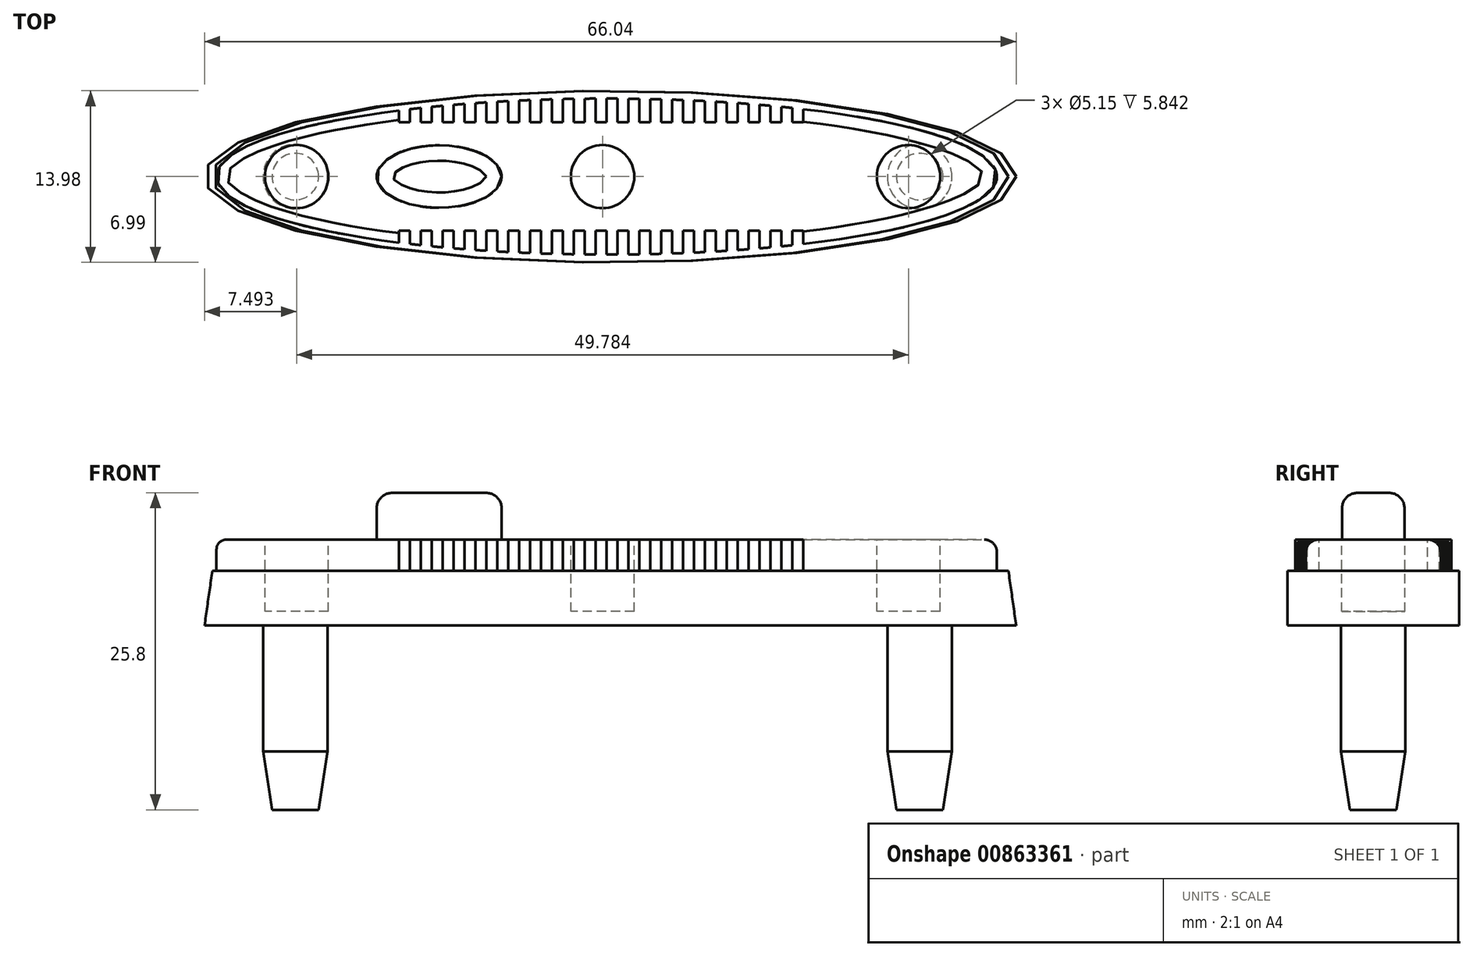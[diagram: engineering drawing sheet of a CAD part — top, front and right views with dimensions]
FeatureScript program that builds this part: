
annotation { "Feature Type Name" : "Feature", "Feature Type Description" : "" }
export const myFeature = defineFeature(function(context is Context, id is Id, definition is map)
    precondition{}
    {
        {
            var Q0;
            Q0=qCreatedBy(makeId("Top.planeOp"),FACE);
            var sketch = newSketch(context, id + "F0", { "sketchPlane" : qUnion([Q0])});
            skEllipse(sketch, "E0", {"center": v(0, 0) * mm, "majorRadius": 33.02 * mm, "minorRadius": 6.99 * mm, "majorAxis": v(1, 0)});
            skSolve(sketch);
        }
        {
            var Q0;
            Q0=qCreatedBy(makeId("Top.planeOp"),FACE);
            cPlane(context, id + "F1", {"entities" : qUnion([Q0]), "cplaneType" : CPlaneType.OFFSET, "offset" : 4.44 * mm, "width" : 152.4 * mm, "height" : 152.4 * mm});
        }
        {
            var Q0;
            Q0=qCreatedBy(id+"F1.planeOp",FACE);
            var sketch = newSketch(context, id + "F2", { "sketchPlane" : qUnion([Q0])});
            skEllipse(sketch, "E1", {"center": v(0, 0) * mm, "majorRadius": 32.39 * mm, "minorRadius": 6.99 * mm, "majorAxis": v(1, 0)});
            skSolve(sketch);
        }
        {
            var Q0;
            Q0=makeQuery(id+"F0.imprint","IMPRINT",FACE,{"disambiguationData":[TD([[makeQuery(id+"F0.imprint","IMPRINT",EDGE,{"derivedFrom":sQuery(id+"F0.wireOp",EDGE,"E0")}),1.0]])]});
            var Q1;
            Q1=makeQuery(id+"F2.imprint","IMPRINT",FACE,{"disambiguationData":[TD([[makeQuery(id+"F2.imprint","IMPRINT",EDGE,{"derivedFrom":sQuery(id+"F2.wireOp",EDGE,"E1")}),1.0]])]});
            loft(context, id + "F3", {"sheetProfilesArray" : [{ "sheetProfileEntities" : qUnion([Q0]) }, { "sheetProfileEntities" : qUnion([Q1]) }]});
        }
        {
            var Q0;
            Q0=makeQuery(id+"F3.opLoft","CAP_FACE",FACE,{"disambiguationData":[OSD([makeQuery(id+"F2.imprint","IMPRINT",FACE,{"disambiguationData":[TD([[makeQuery(id+"F2.imprint","IMPRINT",EDGE,{"derivedFrom":sQuery(id+"F2.wireOp",EDGE,"E1")}),1.0]])]})])],"isStart":true});
            var sketch = newSketch(context, id + "F4", { "sketchPlane" : qUnion([Q0])});
            skEllipse(sketch, "E2", {"center": v(-0.3, 0) * mm, "majorRadius": 31.75 * mm, "minorRadius": 6.35 * mm, "majorAxis": v(-1, 0)});
            skSolve(sketch);
        }
        {
            var Q0;
            Q0=makeQuery(id+"F4.imprint","IMPRINT",FACE,{"disambiguationData":[TD([[makeQuery(id+"F4.imprint","IMPRINT",EDGE,{"derivedFrom":sQuery(id+"F4.wireOp",EDGE,"E2")}),1.0]])]});
            extrude(context, id + "F5", {"entities" : qUnion([Q0]), "operationType" : NewBodyOperationType.ADD, "depth" : 2.54 * mm, "offsetDistance" : 25.4 * mm});
        }
        {
            var Q0;
            Q0=makeQuery(id+"F5.opExtrude","CAP_FACE",FACE,{"disambiguationData":[OSD([sQuery(id+"F4.wireOp",EDGE,"E2")])],"isStart":false});
            var sketch = newSketch(context, id + "F6", { "sketchPlane" : qUnion([Q0])});
            skPoint(sketch, "E3.oppositeSnap0", {"position": v(-0.3, 6.35) * mm});
            skLineSegment(sketch, "E3.bottom", {"start": v(-1.2, 4.4) * mm, "end": v(-0.3, 4.4) * mm});
            skLineSegment(sketch, "E3.top", {"start": v(-1.2, 7.13) * mm, "end": v(-0.3, 7.13) * mm});
            skLineSegment(sketch, "E3.left", {"start": v(-1.2, 4.4) * mm, "end": v(-1.2, 7.13) * mm});
            skLineSegment(sketch, "E3.right", {"start": v(-0.3, 4.4) * mm, "end": v(-0.3, 7.13) * mm});
            skPoint(sketch, "E4.1.0.0", {"position": v(1.48, 6.35) * mm});
            skLineSegment(sketch, "E4.1.0.1", {"start": v(1.48, 4.4) * mm, "end": v(1.48, 7.13) * mm});
            skLineSegment(sketch, "E4.1.0.2", {"start": v(0.57, 4.4) * mm, "end": v(1.48, 4.4) * mm});
            skLineSegment(sketch, "E4.1.0.3", {"start": v(0.57, 4.4) * mm, "end": v(0.57, 7.13) * mm});
            skLineSegment(sketch, "E4.1.0.4", {"start": v(0.57, 7.13) * mm, "end": v(1.48, 7.13) * mm});
            skPoint(sketch, "E4.2.0.0", {"position": v(3.26, 6.35) * mm});
            skLineSegment(sketch, "E4.2.0.1", {"start": v(3.26, 4.4) * mm, "end": v(3.26, 7.13) * mm});
            skLineSegment(sketch, "E4.2.0.2", {"start": v(2.35, 4.4) * mm, "end": v(3.26, 4.4) * mm});
            skLineSegment(sketch, "E4.2.0.3", {"start": v(2.35, 4.4) * mm, "end": v(2.35, 7.13) * mm});
            skLineSegment(sketch, "E4.2.0.4", {"start": v(2.35, 7.13) * mm, "end": v(3.26, 7.13) * mm});
            skPoint(sketch, "E4.3.0.0", {"position": v(5.04, 6.35) * mm});
            skLineSegment(sketch, "E4.3.0.1", {"start": v(5.04, 4.4) * mm, "end": v(5.04, 7.13) * mm});
            skLineSegment(sketch, "E4.3.0.2", {"start": v(4.13, 4.4) * mm, "end": v(5.04, 4.4) * mm});
            skLineSegment(sketch, "E4.3.0.3", {"start": v(4.13, 4.4) * mm, "end": v(4.13, 7.13) * mm});
            skLineSegment(sketch, "E4.3.0.4", {"start": v(4.13, 7.13) * mm, "end": v(5.04, 7.13) * mm});
            skPoint(sketch, "E4.4.0.0", {"position": v(6.81, 6.35) * mm});
            skLineSegment(sketch, "E4.4.0.1", {"start": v(6.81, 4.4) * mm, "end": v(6.81, 7.13) * mm});
            skLineSegment(sketch, "E4.4.0.2", {"start": v(5.9, 4.4) * mm, "end": v(6.81, 4.4) * mm});
            skLineSegment(sketch, "E4.4.0.3", {"start": v(5.9, 4.4) * mm, "end": v(5.9, 7.13) * mm});
            skLineSegment(sketch, "E4.4.0.4", {"start": v(5.9, 7.13) * mm, "end": v(6.81, 7.13) * mm});
            skPoint(sketch, "E4.5.0.0", {"position": v(8.6, 6.35) * mm});
            skLineSegment(sketch, "E4.5.0.1", {"start": v(8.6, 4.4) * mm, "end": v(8.6, 7.13) * mm});
            skLineSegment(sketch, "E4.5.0.2", {"start": v(7.68, 4.4) * mm, "end": v(8.6, 4.4) * mm});
            skLineSegment(sketch, "E4.5.0.3", {"start": v(7.68, 4.4) * mm, "end": v(7.68, 7.13) * mm});
            skLineSegment(sketch, "E4.5.0.4", {"start": v(7.68, 7.13) * mm, "end": v(8.6, 7.13) * mm});
            skPoint(sketch, "E4.6.0.0", {"position": v(10.37, 6.35) * mm});
            skLineSegment(sketch, "E4.6.0.1", {"start": v(10.37, 4.4) * mm, "end": v(10.37, 7.13) * mm});
            skLineSegment(sketch, "E4.6.0.2", {"start": v(9.46, 4.4) * mm, "end": v(10.37, 4.4) * mm});
            skLineSegment(sketch, "E4.6.0.3", {"start": v(9.46, 4.4) * mm, "end": v(9.46, 7.13) * mm});
            skLineSegment(sketch, "E4.6.0.4", {"start": v(9.46, 7.13) * mm, "end": v(10.37, 7.13) * mm});
            skPoint(sketch, "E4.7.0.0", {"position": v(12.15, 6.35) * mm});
            skLineSegment(sketch, "E4.7.0.1", {"start": v(12.15, 4.4) * mm, "end": v(12.15, 7.13) * mm});
            skLineSegment(sketch, "E4.7.0.2", {"start": v(11.24, 4.4) * mm, "end": v(12.15, 4.4) * mm});
            skLineSegment(sketch, "E4.7.0.3", {"start": v(11.24, 4.4) * mm, "end": v(11.24, 7.13) * mm});
            skLineSegment(sketch, "E4.7.0.4", {"start": v(11.24, 7.13) * mm, "end": v(12.15, 7.13) * mm});
            skPoint(sketch, "E4.8.0.0", {"position": v(13.93, 6.35) * mm});
            skLineSegment(sketch, "E4.8.0.1", {"start": v(13.93, 4.4) * mm, "end": v(13.93, 7.13) * mm});
            skLineSegment(sketch, "E4.8.0.2", {"start": v(13.02, 4.4) * mm, "end": v(13.93, 4.4) * mm});
            skLineSegment(sketch, "E4.8.0.3", {"start": v(13.02, 4.4) * mm, "end": v(13.02, 7.13) * mm});
            skLineSegment(sketch, "E4.8.0.4", {"start": v(13.02, 7.13) * mm, "end": v(13.93, 7.13) * mm});
            skPoint(sketch, "E4.9.0.0", {"position": v(15.7, 6.35) * mm});
            skLineSegment(sketch, "E4.9.0.1", {"start": v(15.7, 4.4) * mm, "end": v(15.7, 7.13) * mm});
            skLineSegment(sketch, "E4.9.0.2", {"start": v(14.8, 4.4) * mm, "end": v(15.7, 4.4) * mm});
            skLineSegment(sketch, "E4.9.0.3", {"start": v(14.8, 4.4) * mm, "end": v(14.8, 7.13) * mm});
            skLineSegment(sketch, "E4.9.0.4", {"start": v(14.8, 7.13) * mm, "end": v(15.7, 7.13) * mm});
            skLineSegment(sketch, "E4.direction1", {"start": v(-1.2, 4.4) * mm, "end": v(0.57, 4.4) * mm, "construction": true});
            skLineSegment(sketch, "E5", {"start": v(0, 0) * mm, "end": v(3.55, 0) * mm, "construction": true});
            skLineSegment(sketch, "E6", {"start": v(-0.75, 7.13) * mm, "end": v(-0.75, 4.39) * mm, "construction": true});
            skLineSegment(sketch, "E7.MirrorCS", {"start": v(-0.3, 7.13) * mm, "end": v(-1.2, 7.13) * mm});
            skLineSegment(sketch, "E8.MirrorCS", {"start": v(-5.63, 4.4) * mm, "end": v(-6.54, 4.4) * mm});
            skLineSegment(sketch, "E9.MirrorCS", {"start": v(-14.52, 4.4) * mm, "end": v(-15.43, 4.4) * mm});
            skLineSegment(sketch, "E10.MirrorCS", {"start": v(-16.3, 7.13) * mm, "end": v(-17.21, 7.13) * mm});
            skLineSegment(sketch, "E11.MirrorCS", {"start": v(-3.85, 7.13) * mm, "end": v(-4.76, 7.13) * mm});
            skLineSegment(sketch, "E12.MirrorCS", {"start": v(-9.19, 7.13) * mm, "end": v(-10.1, 7.13) * mm});
            skLineSegment(sketch, "E13.MirrorCS", {"start": v(-2.08, 7.13) * mm, "end": v(-2.99, 7.13) * mm});
            skLineSegment(sketch, "E14.MirrorCS", {"start": v(-16.3, 4.4) * mm, "end": v(-17.21, 4.4) * mm});
            skLineSegment(sketch, "E15.MirrorCS", {"start": v(-12.74, 4.4) * mm, "end": v(-13.65, 4.4) * mm});
            skLineSegment(sketch, "E16.MirrorCS", {"start": v(-14.52, 7.13) * mm, "end": v(-15.43, 7.13) * mm});
            skLineSegment(sketch, "E17.MirrorCS", {"start": v(-9.19, 4.4) * mm, "end": v(-10.1, 4.4) * mm});
            skLineSegment(sketch, "E18.MirrorCS", {"start": v(-12.74, 7.13) * mm, "end": v(-13.65, 7.13) * mm});
            skLineSegment(sketch, "E19.MirrorCS", {"start": v(-10.97, 4.4) * mm, "end": v(-11.88, 4.4) * mm});
            skLineSegment(sketch, "E20.MirrorCS", {"start": v(-3.85, 4.4) * mm, "end": v(-4.76, 4.4) * mm});
            skLineSegment(sketch, "E21.MirrorCS", {"start": v(-7.41, 7.13) * mm, "end": v(-8.32, 7.13) * mm});
            skLineSegment(sketch, "E22.MirrorCS", {"start": v(-7.41, 4.4) * mm, "end": v(-8.32, 4.4) * mm});
            skLineSegment(sketch, "E23.MirrorCS", {"start": v(-2.08, 4.4) * mm, "end": v(-2.99, 4.4) * mm});
            skLineSegment(sketch, "E24.MirrorCS", {"start": v(-10.97, 7.13) * mm, "end": v(-11.88, 7.13) * mm});
            skLineSegment(sketch, "E25.MirrorCS", {"start": v(-5.63, 7.13) * mm, "end": v(-6.54, 7.13) * mm});
            skLineSegment(sketch, "E26.MirrorCS", {"start": v(-6.54, 4.4) * mm, "end": v(-6.54, 7.13) * mm});
            skLineSegment(sketch, "E27.MirrorCS", {"start": v(-2.99, 4.4) * mm, "end": v(-2.99, 7.13) * mm});
            skLineSegment(sketch, "E28.MirrorCS", {"start": v(-15.43, 4.4) * mm, "end": v(-15.43, 7.13) * mm});
            skLineSegment(sketch, "E29.MirrorCS", {"start": v(-9.19, 4.4) * mm, "end": v(-9.19, 7.13) * mm});
            skLineSegment(sketch, "E30.MirrorCS", {"start": v(-8.32, 4.4) * mm, "end": v(-8.32, 7.13) * mm});
            skLineSegment(sketch, "E31.MirrorCS", {"start": v(-11.88, 4.4) * mm, "end": v(-11.88, 7.13) * mm});
            skLineSegment(sketch, "E32.MirrorCS", {"start": v(-4.76, 4.4) * mm, "end": v(-4.76, 7.13) * mm});
            skLineSegment(sketch, "E33.MirrorCS", {"start": v(-10.1, 4.4) * mm, "end": v(-10.1, 7.13) * mm});
            skLineSegment(sketch, "E34.MirrorCS", {"start": v(-13.65, 4.4) * mm, "end": v(-13.65, 7.13) * mm});
            skLineSegment(sketch, "E35.MirrorCS", {"start": v(-17.21, 4.4) * mm, "end": v(-17.21, 7.13) * mm});
            skPoint(sketch, "E36.MirrorP", {"position": v(-15.43, 6.35) * mm});
            skLineSegment(sketch, "E37.MirrorCS", {"start": v(-2.08, 4.4) * mm, "end": v(-2.08, 7.13) * mm});
            skPoint(sketch, "E38.MirrorP", {"position": v(-4.76, 6.35) * mm});
            skLineSegment(sketch, "E39.MirrorCS", {"start": v(-12.74, 4.4) * mm, "end": v(-12.74, 7.13) * mm});
            skPoint(sketch, "E40.MirrorP", {"position": v(-11.88, 6.35) * mm});
            skPoint(sketch, "E41.MirrorP", {"position": v(-2.99, 6.35) * mm});
            skLineSegment(sketch, "E42.MirrorCS", {"start": v(-16.3, 4.4) * mm, "end": v(-16.3, 7.13) * mm});
            skPoint(sketch, "E43.MirrorP", {"position": v(-6.54, 6.35) * mm});
            skPoint(sketch, "E44.MirrorP", {"position": v(-1.2, 6.35) * mm});
            skLineSegment(sketch, "E45.MirrorCS", {"start": v(-5.63, 4.4) * mm, "end": v(-5.63, 7.13) * mm});
            skLineSegment(sketch, "E46.MirrorCS", {"start": v(-7.41, 4.4) * mm, "end": v(-7.41, 7.13) * mm});
            skPoint(sketch, "E47.MirrorP", {"position": v(-10.1, 6.35) * mm});
            skLineSegment(sketch, "E48.MirrorCS", {"start": v(-14.52, 4.4) * mm, "end": v(-14.52, 7.13) * mm});
            skLineSegment(sketch, "E49.MirrorCS", {"start": v(-3.85, 4.4) * mm, "end": v(-3.85, 7.13) * mm});
            skPoint(sketch, "E50.MirrorP", {"position": v(-8.32, 6.35) * mm});
            skPoint(sketch, "E51.MirrorP", {"position": v(-13.65, 6.35) * mm});
            skPoint(sketch, "E52.MirrorP", {"position": v(-17.21, 6.35) * mm});
            skLineSegment(sketch, "E53.MirrorCS", {"start": v(-10.97, 4.4) * mm, "end": v(-10.97, 7.13) * mm});
            skLineSegment(sketch, "E54.MirrorCS", {"start": v(-0.3, -7.13) * mm, "end": v(-1.2, -7.13) * mm});
            skLineSegment(sketch, "E55.MirrorCS", {"start": v(-1.2, -7.13) * mm, "end": v(-0.3, -7.13) * mm});
            skLineSegment(sketch, "E56.MirrorCS", {"start": v(-0.75, -7.13) * mm, "end": v(-0.75, -4.39) * mm, "construction": true});
            skLineSegment(sketch, "E57.MirrorCS", {"start": v(2.35, -7.13) * mm, "end": v(3.26, -7.13) * mm});
            skLineSegment(sketch, "E58.MirrorCS", {"start": v(2.35, -4.4) * mm, "end": v(3.26, -4.4) * mm});
            skLineSegment(sketch, "E59.MirrorCS", {"start": v(7.68, -7.13) * mm, "end": v(8.6, -7.13) * mm});
            skLineSegment(sketch, "E60.MirrorCS", {"start": v(0.57, -7.13) * mm, "end": v(1.48, -7.13) * mm});
            skLineSegment(sketch, "E61.MirrorCS", {"start": v(14.8, -7.13) * mm, "end": v(15.7, -7.13) * mm});
            skLineSegment(sketch, "E62.MirrorCS", {"start": v(-12.74, -7.13) * mm, "end": v(-13.65, -7.13) * mm});
            skLineSegment(sketch, "E63.MirrorCS", {"start": v(0.57, -4.4) * mm, "end": v(1.48, -4.4) * mm});
            skLineSegment(sketch, "E64.MirrorCS", {"start": v(-1.2, -4.4) * mm, "end": v(-0.3, -4.4) * mm});
            skLineSegment(sketch, "E65.MirrorCS", {"start": v(-2.08, -7.13) * mm, "end": v(-2.99, -7.13) * mm});
            skLineSegment(sketch, "E66.MirrorCS", {"start": v(11.24, -4.4) * mm, "end": v(12.15, -4.4) * mm});
            skLineSegment(sketch, "E67.MirrorCS", {"start": v(-12.74, -4.4) * mm, "end": v(-13.65, -4.4) * mm});
            skLineSegment(sketch, "E68.MirrorCS", {"start": v(-5.63, -4.4) * mm, "end": v(-6.54, -4.4) * mm});
            skLineSegment(sketch, "E69.MirrorCS", {"start": v(-10.97, -7.13) * mm, "end": v(-11.88, -7.13) * mm});
            skLineSegment(sketch, "E70.MirrorCS", {"start": v(-10.97, -4.4) * mm, "end": v(-11.88, -4.4) * mm});
            skLineSegment(sketch, "E71.MirrorCS", {"start": v(13.02, -7.13) * mm, "end": v(13.93, -7.13) * mm});
            skLineSegment(sketch, "E72.MirrorCS", {"start": v(9.46, -4.4) * mm, "end": v(10.37, -4.4) * mm});
            skLineSegment(sketch, "E73.MirrorCS", {"start": v(-7.41, -7.13) * mm, "end": v(-8.32, -7.13) * mm});
            skLineSegment(sketch, "E74.MirrorCS", {"start": v(4.13, -4.4) * mm, "end": v(5.04, -4.4) * mm});
            skLineSegment(sketch, "E75.MirrorCS", {"start": v(-3.85, -4.4) * mm, "end": v(-4.76, -4.4) * mm});
            skLineSegment(sketch, "E76.MirrorCS", {"start": v(-14.52, -7.13) * mm, "end": v(-15.43, -7.13) * mm});
            skLineSegment(sketch, "E77.MirrorCS", {"start": v(-16.3, -4.4) * mm, "end": v(-17.21, -4.4) * mm});
            skLineSegment(sketch, "E78.MirrorCS", {"start": v(7.68, -4.4) * mm, "end": v(8.6, -4.4) * mm});
            skLineSegment(sketch, "E79.MirrorCS", {"start": v(-7.41, -4.4) * mm, "end": v(-8.32, -4.4) * mm});
            skLineSegment(sketch, "E80.MirrorCS", {"start": v(-9.19, -4.4) * mm, "end": v(-10.1, -4.4) * mm});
            skLineSegment(sketch, "E81.MirrorCS", {"start": v(-1.2, -4.4) * mm, "end": v(0.57, -4.4) * mm, "construction": true});
            skLineSegment(sketch, "E82.MirrorCS", {"start": v(13.02, -4.4) * mm, "end": v(13.93, -4.4) * mm});
            skLineSegment(sketch, "E83.MirrorCS", {"start": v(-2.08, -4.4) * mm, "end": v(-2.99, -4.4) * mm});
            skLineSegment(sketch, "E84.MirrorCS", {"start": v(5.9, -7.13) * mm, "end": v(6.81, -7.13) * mm});
            skLineSegment(sketch, "E85.MirrorCS", {"start": v(11.24, -7.13) * mm, "end": v(12.15, -7.13) * mm});
            skLineSegment(sketch, "E86.MirrorCS", {"start": v(-14.52, -4.4) * mm, "end": v(-15.43, -4.4) * mm});
            skLineSegment(sketch, "E87.MirrorCS", {"start": v(-1.2, -4.4) * mm, "end": v(-1.2, -7.13) * mm});
            skLineSegment(sketch, "E88.MirrorCS", {"start": v(-9.19, -7.13) * mm, "end": v(-10.1, -7.13) * mm});
            skLineSegment(sketch, "E89.MirrorCS", {"start": v(-16.3, -7.13) * mm, "end": v(-17.21, -7.13) * mm});
            skLineSegment(sketch, "E90.MirrorCS", {"start": v(14.8, -4.4) * mm, "end": v(15.7, -4.4) * mm});
            skLineSegment(sketch, "E91.MirrorCS", {"start": v(5.9, -4.4) * mm, "end": v(6.81, -4.4) * mm});
            skLineSegment(sketch, "E92.MirrorCS", {"start": v(-3.85, -7.13) * mm, "end": v(-4.76, -7.13) * mm});
            skLineSegment(sketch, "E93.MirrorCS", {"start": v(4.13, -7.13) * mm, "end": v(5.04, -7.13) * mm});
            skLineSegment(sketch, "E94.MirrorCS", {"start": v(9.46, -7.13) * mm, "end": v(10.37, -7.13) * mm});
            skLineSegment(sketch, "E95.MirrorCS", {"start": v(-5.63, -7.13) * mm, "end": v(-6.54, -7.13) * mm});
            skLineSegment(sketch, "E96.MirrorCS", {"start": v(5.04, -4.4) * mm, "end": v(5.04, -7.13) * mm});
            skLineSegment(sketch, "E97.MirrorCS", {"start": v(-13.65, -4.4) * mm, "end": v(-13.65, -7.13) * mm});
            skLineSegment(sketch, "E98.MirrorCS", {"start": v(3.26, -4.4) * mm, "end": v(3.26, -7.13) * mm});
            skLineSegment(sketch, "E99.MirrorCS", {"start": v(1.48, -4.4) * mm, "end": v(1.48, -7.13) * mm});
            skLineSegment(sketch, "E100.MirrorCS", {"start": v(-0.3, -4.4) * mm, "end": v(-0.3, -7.13) * mm});
            skLineSegment(sketch, "E101.MirrorCS", {"start": v(15.7, -4.4) * mm, "end": v(15.7, -7.13) * mm});
            skLineSegment(sketch, "E102.MirrorCS", {"start": v(-11.88, -4.4) * mm, "end": v(-11.88, -7.13) * mm});
            skLineSegment(sketch, "E103.MirrorCS", {"start": v(-7.41, -4.4) * mm, "end": v(-7.41, -7.13) * mm});
            skLineSegment(sketch, "E104.MirrorCS", {"start": v(8.6, -4.4) * mm, "end": v(8.6, -7.13) * mm});
            skLineSegment(sketch, "E105.MirrorCS", {"start": v(-17.21, -4.4) * mm, "end": v(-17.21, -7.13) * mm});
            skLineSegment(sketch, "E106.MirrorCS", {"start": v(-8.32, -4.4) * mm, "end": v(-8.32, -7.13) * mm});
            skLineSegment(sketch, "E107.MirrorCS", {"start": v(12.15, -4.4) * mm, "end": v(12.15, -7.13) * mm});
            skLineSegment(sketch, "E108.MirrorCS", {"start": v(6.81, -4.4) * mm, "end": v(6.81, -7.13) * mm});
            skLineSegment(sketch, "E109.MirrorCS", {"start": v(-10.1, -4.4) * mm, "end": v(-10.1, -7.13) * mm});
            skLineSegment(sketch, "E110.MirrorCS", {"start": v(-15.43, -4.4) * mm, "end": v(-15.43, -7.13) * mm});
            skLineSegment(sketch, "E111.MirrorCS", {"start": v(-2.99, -4.4) * mm, "end": v(-2.99, -7.13) * mm});
            skLineSegment(sketch, "E112.MirrorCS", {"start": v(10.37, -4.4) * mm, "end": v(10.37, -7.13) * mm});
            skLineSegment(sketch, "E113.MirrorCS", {"start": v(13.93, -4.4) * mm, "end": v(13.93, -7.13) * mm});
            skLineSegment(sketch, "E114.MirrorCS", {"start": v(-4.76, -4.4) * mm, "end": v(-4.76, -7.13) * mm});
            skLineSegment(sketch, "E115.MirrorCS", {"start": v(-6.54, -4.4) * mm, "end": v(-6.54, -7.13) * mm});
            skLineSegment(sketch, "E116.MirrorCS", {"start": v(2.35, -4.4) * mm, "end": v(2.35, -7.13) * mm});
            skPoint(sketch, "E117.MirrorP", {"position": v(10.37, -6.35) * mm});
            skLineSegment(sketch, "E118.MirrorCS", {"start": v(0.57, -4.4) * mm, "end": v(0.57, -7.13) * mm});
            skLineSegment(sketch, "E119.MirrorCS", {"start": v(13.02, -4.4) * mm, "end": v(13.02, -7.13) * mm});
            skLineSegment(sketch, "E120.MirrorCS", {"start": v(-9.19, -4.4) * mm, "end": v(-9.19, -7.13) * mm});
            skPoint(sketch, "E121.MirrorP", {"position": v(1.48, -6.35) * mm});
            skPoint(sketch, "E122.MirrorP", {"position": v(-17.21, -6.35) * mm});
            skPoint(sketch, "E123.MirrorP", {"position": v(-11.88, -6.35) * mm});
            skLineSegment(sketch, "E124.MirrorCS", {"start": v(5.9, -4.4) * mm, "end": v(5.9, -7.13) * mm});
            skPoint(sketch, "E125.MirrorP", {"position": v(5.04, -6.35) * mm});
            skLineSegment(sketch, "E126.MirrorCS", {"start": v(4.13, -4.4) * mm, "end": v(4.13, -7.13) * mm});
            skLineSegment(sketch, "E127.MirrorCS", {"start": v(7.68, -4.4) * mm, "end": v(7.68, -7.13) * mm});
            skPoint(sketch, "E128.MirrorP", {"position": v(13.93, -6.35) * mm});
            skPoint(sketch, "E129.MirrorP", {"position": v(-4.76, -6.35) * mm});
            skPoint(sketch, "E130.MirrorP", {"position": v(-15.43, -6.35) * mm});
            skLineSegment(sketch, "E131.MirrorCS", {"start": v(-3.85, -4.4) * mm, "end": v(-3.85, -7.13) * mm});
            skPoint(sketch, "E132.MirrorP", {"position": v(15.7, -6.35) * mm});
            skPoint(sketch, "E133.MirrorP", {"position": v(-8.32, -6.35) * mm});
            skPoint(sketch, "E134.MirrorP", {"position": v(-0.3, -6.35) * mm});
            skPoint(sketch, "E135.MirrorP", {"position": v(-2.99, -6.35) * mm});
            skPoint(sketch, "E136.MirrorP", {"position": v(-6.54, -6.35) * mm});
            skPoint(sketch, "E137.MirrorP", {"position": v(12.15, -6.35) * mm});
            skLineSegment(sketch, "E138.MirrorCS", {"start": v(11.24, -4.4) * mm, "end": v(11.24, -7.13) * mm});
            skPoint(sketch, "E139.MirrorP", {"position": v(-10.1, -6.35) * mm});
            skLineSegment(sketch, "E140.MirrorCS", {"start": v(-10.97, -4.4) * mm, "end": v(-10.97, -7.13) * mm});
            skPoint(sketch, "E141.MirrorP", {"position": v(6.81, -6.35) * mm});
            skLineSegment(sketch, "E142.MirrorCS", {"start": v(-5.63, -4.4) * mm, "end": v(-5.63, -7.13) * mm});
            skPoint(sketch, "E143.MirrorP", {"position": v(-1.2, -6.35) * mm});
            skPoint(sketch, "E144.MirrorP", {"position": v(8.6, -6.35) * mm});
            skPoint(sketch, "E145.MirrorP", {"position": v(-13.65, -6.35) * mm});
            skLineSegment(sketch, "E146.MirrorCS", {"start": v(-2.08, -4.4) * mm, "end": v(-2.08, -7.13) * mm});
            skPoint(sketch, "E147.MirrorP", {"position": v(3.26, -6.35) * mm});
            skLineSegment(sketch, "E148.MirrorCS", {"start": v(9.46, -4.4) * mm, "end": v(9.46, -7.13) * mm});
            skLineSegment(sketch, "E149.MirrorCS", {"start": v(14.8, -4.4) * mm, "end": v(14.8, -7.13) * mm});
            skLineSegment(sketch, "E150.MirrorCS", {"start": v(-12.74, -4.4) * mm, "end": v(-12.74, -7.13) * mm});
            skLineSegment(sketch, "E151.MirrorCS", {"start": v(-14.52, -4.4) * mm, "end": v(-14.52, -7.13) * mm});
            skLineSegment(sketch, "E152.MirrorCS", {"start": v(-16.3, -4.4) * mm, "end": v(-16.3, -7.13) * mm});
            skSolve(sketch);
        }
        {
            var Q0;
            {var subQ0=sQuery(id+"F6.wireOp",EDGE,"E14.MirrorCS");Q0=makeQuery(id+"F6.imprint","IMPRINT",FACE,{"disambiguationData":[TD([[makeQuery(id+"F6.imprint","IMPRINT",EDGE,{"derivedFrom":subQ0}),-1.0]])]});}
            var Q1;
            {var subQ0=sQuery(id+"F6.wireOp",EDGE,"E9.MirrorCS");Q1=makeQuery(id+"F6.imprint","IMPRINT",FACE,{"disambiguationData":[TD([[makeQuery(id+"F6.imprint","IMPRINT",EDGE,{"derivedFrom":subQ0}),-1.0]])]});}
            var Q2;
            {var subQ0=sQuery(id+"F6.wireOp",EDGE,"E15.MirrorCS");Q2=makeQuery(id+"F6.imprint","IMPRINT",FACE,{"disambiguationData":[TD([[makeQuery(id+"F6.imprint","IMPRINT",EDGE,{"derivedFrom":subQ0}),-1.0]])]});}
            var Q3;
            {var subQ0=sQuery(id+"F6.wireOp",EDGE,"E19.MirrorCS");Q3=makeQuery(id+"F6.imprint","IMPRINT",FACE,{"disambiguationData":[TD([[makeQuery(id+"F6.imprint","IMPRINT",EDGE,{"derivedFrom":subQ0}),-1.0]])]});}
            var Q4;
            {var subQ0=sQuery(id+"F6.wireOp",EDGE,"E17.MirrorCS");Q4=makeQuery(id+"F6.imprint","IMPRINT",FACE,{"disambiguationData":[TD([[makeQuery(id+"F6.imprint","IMPRINT",EDGE,{"derivedFrom":subQ0}),-1.0]])]});}
            var Q5;
            {var subQ0=sQuery(id+"F6.wireOp",EDGE,"E22.MirrorCS");Q5=makeQuery(id+"F6.imprint","IMPRINT",FACE,{"disambiguationData":[TD([[makeQuery(id+"F6.imprint","IMPRINT",EDGE,{"derivedFrom":subQ0}),-1.0]])]});}
            var Q6;
            {var subQ0=sQuery(id+"F6.wireOp",EDGE,"E8.MirrorCS");Q6=makeQuery(id+"F6.imprint","IMPRINT",FACE,{"disambiguationData":[TD([[makeQuery(id+"F6.imprint","IMPRINT",EDGE,{"derivedFrom":subQ0}),-1.0]])]});}
            var Q7;
            {var subQ0=sQuery(id+"F6.wireOp",EDGE,"E20.MirrorCS");Q7=makeQuery(id+"F6.imprint","IMPRINT",FACE,{"disambiguationData":[TD([[makeQuery(id+"F6.imprint","IMPRINT",EDGE,{"derivedFrom":subQ0}),-1.0]])]});}
            var Q8;
            {var subQ0=sQuery(id+"F6.wireOp",EDGE,"E23.MirrorCS");Q8=makeQuery(id+"F6.imprint","IMPRINT",FACE,{"disambiguationData":[TD([[makeQuery(id+"F6.imprint","IMPRINT",EDGE,{"derivedFrom":subQ0}),-1.0]])]});}
            var Q9;
            {var subQ0=sQuery(id+"F6.wireOp",EDGE,"E3.bottom");Q9=makeQuery(id+"F6.imprint","IMPRINT",FACE,{"disambiguationData":[TD([[makeQuery(id+"F6.imprint","IMPRINT",EDGE,{"derivedFrom":subQ0}),1.0]])]});}
            var Q10;
            {var subQ0=sQuery(id+"F6.wireOp",EDGE,"E4.1.0.2");Q10=makeQuery(id+"F6.imprint","IMPRINT",FACE,{"disambiguationData":[TD([[makeQuery(id+"F6.imprint","IMPRINT",EDGE,{"derivedFrom":subQ0}),1.0]])]});}
            var Q11;
            {var subQ0=sQuery(id+"F6.wireOp",EDGE,"E4.2.0.2");Q11=makeQuery(id+"F6.imprint","IMPRINT",FACE,{"disambiguationData":[TD([[makeQuery(id+"F6.imprint","IMPRINT",EDGE,{"derivedFrom":subQ0}),1.0]])]});}
            var Q12;
            {var subQ0=sQuery(id+"F6.wireOp",EDGE,"E4.3.0.2");Q12=makeQuery(id+"F6.imprint","IMPRINT",FACE,{"disambiguationData":[TD([[makeQuery(id+"F6.imprint","IMPRINT",EDGE,{"derivedFrom":subQ0}),1.0]])]});}
            var Q13;
            {var subQ0=sQuery(id+"F6.wireOp",EDGE,"E4.4.0.2");Q13=makeQuery(id+"F6.imprint","IMPRINT",FACE,{"disambiguationData":[TD([[makeQuery(id+"F6.imprint","IMPRINT",EDGE,{"derivedFrom":subQ0}),1.0]])]});}
            var Q14;
            {var subQ0=sQuery(id+"F6.wireOp",EDGE,"E4.5.0.2");Q14=makeQuery(id+"F6.imprint","IMPRINT",FACE,{"disambiguationData":[TD([[makeQuery(id+"F6.imprint","IMPRINT",EDGE,{"derivedFrom":subQ0}),1.0]])]});}
            var Q15;
            {var subQ0=sQuery(id+"F6.wireOp",EDGE,"E4.6.0.2");Q15=makeQuery(id+"F6.imprint","IMPRINT",FACE,{"disambiguationData":[TD([[makeQuery(id+"F6.imprint","IMPRINT",EDGE,{"derivedFrom":subQ0}),1.0]])]});}
            var Q16;
            {var subQ0=sQuery(id+"F6.wireOp",EDGE,"E4.7.0.2");Q16=makeQuery(id+"F6.imprint","IMPRINT",FACE,{"disambiguationData":[TD([[makeQuery(id+"F6.imprint","IMPRINT",EDGE,{"derivedFrom":subQ0}),1.0]])]});}
            var Q17;
            {var subQ0=sQuery(id+"F6.wireOp",EDGE,"E4.8.0.2");Q17=makeQuery(id+"F6.imprint","IMPRINT",FACE,{"disambiguationData":[TD([[makeQuery(id+"F6.imprint","IMPRINT",EDGE,{"derivedFrom":subQ0}),1.0]])]});}
            var Q18;
            {var subQ0=sQuery(id+"F6.wireOp",EDGE,"E4.9.0.2");Q18=makeQuery(id+"F6.imprint","IMPRINT",FACE,{"disambiguationData":[TD([[makeQuery(id+"F6.imprint","IMPRINT",EDGE,{"derivedFrom":subQ0}),1.0]])]});}
            var Q19;
            {var subQ0=sQuery(id+"F6.wireOp",EDGE,"E77.MirrorCS");Q19=makeQuery(id+"F6.imprint","IMPRINT",FACE,{"disambiguationData":[TD([[makeQuery(id+"F6.imprint","IMPRINT",EDGE,{"derivedFrom":subQ0}),1.0]])]});}
            var Q20;
            {var subQ0=sQuery(id+"F6.wireOp",EDGE,"E86.MirrorCS");Q20=makeQuery(id+"F6.imprint","IMPRINT",FACE,{"disambiguationData":[TD([[makeQuery(id+"F6.imprint","IMPRINT",EDGE,{"derivedFrom":subQ0}),1.0]])]});}
            var Q21;
            {var subQ0=sQuery(id+"F6.wireOp",EDGE,"E67.MirrorCS");Q21=makeQuery(id+"F6.imprint","IMPRINT",FACE,{"disambiguationData":[TD([[makeQuery(id+"F6.imprint","IMPRINT",EDGE,{"derivedFrom":subQ0}),1.0]])]});}
            var Q22;
            {var subQ0=sQuery(id+"F6.wireOp",EDGE,"E70.MirrorCS");Q22=makeQuery(id+"F6.imprint","IMPRINT",FACE,{"disambiguationData":[TD([[makeQuery(id+"F6.imprint","IMPRINT",EDGE,{"derivedFrom":subQ0}),1.0]])]});}
            var Q23;
            {var subQ0=sQuery(id+"F6.wireOp",EDGE,"E80.MirrorCS");Q23=makeQuery(id+"F6.imprint","IMPRINT",FACE,{"disambiguationData":[TD([[makeQuery(id+"F6.imprint","IMPRINT",EDGE,{"derivedFrom":subQ0}),1.0]])]});}
            var Q24;
            {var subQ0=sQuery(id+"F6.wireOp",EDGE,"E79.MirrorCS");Q24=makeQuery(id+"F6.imprint","IMPRINT",FACE,{"disambiguationData":[TD([[makeQuery(id+"F6.imprint","IMPRINT",EDGE,{"derivedFrom":subQ0}),1.0]])]});}
            var Q25;
            {var subQ0=sQuery(id+"F6.wireOp",EDGE,"E68.MirrorCS");Q25=makeQuery(id+"F6.imprint","IMPRINT",FACE,{"disambiguationData":[TD([[makeQuery(id+"F6.imprint","IMPRINT",EDGE,{"derivedFrom":subQ0}),1.0]])]});}
            var Q26;
            {var subQ0=sQuery(id+"F6.wireOp",EDGE,"E75.MirrorCS");Q26=makeQuery(id+"F6.imprint","IMPRINT",FACE,{"disambiguationData":[TD([[makeQuery(id+"F6.imprint","IMPRINT",EDGE,{"derivedFrom":subQ0}),1.0]])]});}
            var Q27;
            {var subQ0=sQuery(id+"F6.wireOp",EDGE,"E83.MirrorCS");Q27=makeQuery(id+"F6.imprint","IMPRINT",FACE,{"disambiguationData":[TD([[makeQuery(id+"F6.imprint","IMPRINT",EDGE,{"derivedFrom":subQ0}),1.0]])]});}
            var Q28;
            {var subQ0=sQuery(id+"F6.wireOp",EDGE,"E64.MirrorCS");Q28=makeQuery(id+"F6.imprint","IMPRINT",FACE,{"disambiguationData":[TD([[makeQuery(id+"F6.imprint","IMPRINT",EDGE,{"derivedFrom":subQ0}),-1.0]])]});}
            var Q29;
            {var subQ0=sQuery(id+"F6.wireOp",EDGE,"E63.MirrorCS");Q29=makeQuery(id+"F6.imprint","IMPRINT",FACE,{"disambiguationData":[TD([[makeQuery(id+"F6.imprint","IMPRINT",EDGE,{"derivedFrom":subQ0}),-1.0]])]});}
            var Q30;
            {var subQ0=sQuery(id+"F6.wireOp",EDGE,"E58.MirrorCS");Q30=makeQuery(id+"F6.imprint","IMPRINT",FACE,{"disambiguationData":[TD([[makeQuery(id+"F6.imprint","IMPRINT",EDGE,{"derivedFrom":subQ0}),-1.0]])]});}
            var Q31;
            {var subQ0=sQuery(id+"F6.wireOp",EDGE,"E74.MirrorCS");Q31=makeQuery(id+"F6.imprint","IMPRINT",FACE,{"disambiguationData":[TD([[makeQuery(id+"F6.imprint","IMPRINT",EDGE,{"derivedFrom":subQ0}),-1.0]])]});}
            var Q32;
            {var subQ0=sQuery(id+"F6.wireOp",EDGE,"E91.MirrorCS");Q32=makeQuery(id+"F6.imprint","IMPRINT",FACE,{"disambiguationData":[TD([[makeQuery(id+"F6.imprint","IMPRINT",EDGE,{"derivedFrom":subQ0}),-1.0]])]});}
            var Q33;
            {var subQ0=sQuery(id+"F6.wireOp",EDGE,"E78.MirrorCS");Q33=makeQuery(id+"F6.imprint","IMPRINT",FACE,{"disambiguationData":[TD([[makeQuery(id+"F6.imprint","IMPRINT",EDGE,{"derivedFrom":subQ0}),-1.0]])]});}
            var Q34;
            {var subQ0=sQuery(id+"F6.wireOp",EDGE,"E72.MirrorCS");Q34=makeQuery(id+"F6.imprint","IMPRINT",FACE,{"disambiguationData":[TD([[makeQuery(id+"F6.imprint","IMPRINT",EDGE,{"derivedFrom":subQ0}),-1.0]])]});}
            var Q35;
            {var subQ0=sQuery(id+"F6.wireOp",EDGE,"E66.MirrorCS");Q35=makeQuery(id+"F6.imprint","IMPRINT",FACE,{"disambiguationData":[TD([[makeQuery(id+"F6.imprint","IMPRINT",EDGE,{"derivedFrom":subQ0}),-1.0]])]});}
            var Q36;
            {var subQ0=sQuery(id+"F6.wireOp",EDGE,"E82.MirrorCS");Q36=makeQuery(id+"F6.imprint","IMPRINT",FACE,{"disambiguationData":[TD([[makeQuery(id+"F6.imprint","IMPRINT",EDGE,{"derivedFrom":subQ0}),-1.0]])]});}
            var Q37;
            {var subQ0=sQuery(id+"F6.wireOp",EDGE,"E90.MirrorCS");Q37=makeQuery(id+"F6.imprint","IMPRINT",FACE,{"disambiguationData":[TD([[makeQuery(id+"F6.imprint","IMPRINT",EDGE,{"derivedFrom":subQ0}),-1.0]])]});}
            extrude(context, id + "F7", {"entities" : qUnion([Q0, Q1, Q2, Q3, Q4, Q5, Q6, Q7, Q8, Q9, Q10, Q11, Q12, Q13, Q14, Q15, Q16, Q17, Q18, Q19, Q20, Q21, Q22, Q23, Q24, Q25, Q26, Q27, Q28, Q29, Q30, Q31, Q32, Q33, Q34, Q35, Q36, Q37]), "operationType" : NewBodyOperationType.REMOVE, "oppositeDirection" : true, "depth" : 2.54 * mm, "offsetDistance" : 25.4 * mm});
        }
        {
            var Q0;
            {var subQ0=sQuery(id+"F4.wireOp",EDGE,"E2");Q0=makeQuery(id+"F7.boolean.opBoolean","SPLIT",EDGE,{"disambiguationData":[TD([makeQuery(id+"F7.opExtrude","SWEPT_FACE",FACE,{"disambiguationData":[OSD([sQuery(id+"F6.wireOp",EDGE,"E4.9.0.1")])]})])],"derivedFrom":makeQuery(id+"F5.opExtrude","CAP_EDGE",EDGE,{"disambiguationData":[OSD([subQ0])],"isStart":false})});}
            var Q1;
            {var subQ0=sQuery(id+"F4.wireOp",EDGE,"E2");Q1=makeQuery(id+"F7.boolean.opBoolean","SPLIT",EDGE,{"disambiguationData":[TD([makeQuery(id+"F7.opExtrude","SWEPT_FACE",FACE,{"disambiguationData":[OSD([sQuery(id+"F6.wireOp",EDGE,"E4.8.0.1")])]})])],"derivedFrom":makeQuery(id+"F5.opExtrude","CAP_EDGE",EDGE,{"disambiguationData":[OSD([subQ0])],"isStart":false})});}
            var Q2;
            {var subQ0=sQuery(id+"F4.wireOp",EDGE,"E2");Q2=makeQuery(id+"F7.boolean.opBoolean","SPLIT",EDGE,{"disambiguationData":[TD([makeQuery(id+"F7.opExtrude","SWEPT_FACE",FACE,{"disambiguationData":[OSD([sQuery(id+"F6.wireOp",EDGE,"E113.MirrorCS")])]})])],"derivedFrom":makeQuery(id+"F5.opExtrude","CAP_EDGE",EDGE,{"disambiguationData":[OSD([subQ0])],"isStart":false})});}
            var Q3;
            {var subQ0=sQuery(id+"F4.wireOp",EDGE,"E2");Q3=makeQuery(id+"F7.boolean.opBoolean","SPLIT",EDGE,{"disambiguationData":[TD([makeQuery(id+"F7.opExtrude","SWEPT_FACE",FACE,{"disambiguationData":[OSD([sQuery(id+"F6.wireOp",EDGE,"E4.7.0.1")])]})])],"derivedFrom":makeQuery(id+"F5.opExtrude","CAP_EDGE",EDGE,{"disambiguationData":[OSD([subQ0])],"isStart":false})});}
            var Q4;
            {var subQ0=sQuery(id+"F4.wireOp",EDGE,"E2");Q4=makeQuery(id+"F7.boolean.opBoolean","SPLIT",EDGE,{"disambiguationData":[TD([makeQuery(id+"F7.opExtrude","SWEPT_FACE",FACE,{"disambiguationData":[OSD([sQuery(id+"F6.wireOp",EDGE,"E107.MirrorCS")])]})])],"derivedFrom":makeQuery(id+"F5.opExtrude","CAP_EDGE",EDGE,{"disambiguationData":[OSD([subQ0])],"isStart":false})});}
            var Q5;
            {var subQ0=sQuery(id+"F4.wireOp",EDGE,"E2");Q5=makeQuery(id+"F7.boolean.opBoolean","SPLIT",EDGE,{"disambiguationData":[TD([makeQuery(id+"F7.opExtrude","SWEPT_FACE",FACE,{"disambiguationData":[OSD([sQuery(id+"F6.wireOp",EDGE,"E4.6.0.1")])]})])],"derivedFrom":makeQuery(id+"F5.opExtrude","CAP_EDGE",EDGE,{"disambiguationData":[OSD([subQ0])],"isStart":false})});}
            var Q6;
            {var subQ0=sQuery(id+"F4.wireOp",EDGE,"E2");Q6=makeQuery(id+"F7.boolean.opBoolean","SPLIT",EDGE,{"disambiguationData":[TD([makeQuery(id+"F7.opExtrude","SWEPT_FACE",FACE,{"disambiguationData":[OSD([sQuery(id+"F6.wireOp",EDGE,"E112.MirrorCS")])]})])],"derivedFrom":makeQuery(id+"F5.opExtrude","CAP_EDGE",EDGE,{"disambiguationData":[OSD([subQ0])],"isStart":false})});}
            var Q7;
            {var subQ0=sQuery(id+"F4.wireOp",EDGE,"E2");Q7=makeQuery(id+"F7.boolean.opBoolean","SPLIT",EDGE,{"disambiguationData":[TD([makeQuery(id+"F7.opExtrude","SWEPT_FACE",FACE,{"disambiguationData":[OSD([sQuery(id+"F6.wireOp",EDGE,"E4.5.0.1")])]})])],"derivedFrom":makeQuery(id+"F5.opExtrude","CAP_EDGE",EDGE,{"disambiguationData":[OSD([subQ0])],"isStart":false})});}
            var Q8;
            {var subQ0=sQuery(id+"F4.wireOp",EDGE,"E2");Q8=makeQuery(id+"F7.boolean.opBoolean","SPLIT",EDGE,{"disambiguationData":[TD([makeQuery(id+"F7.opExtrude","SWEPT_FACE",FACE,{"disambiguationData":[OSD([sQuery(id+"F6.wireOp",EDGE,"E104.MirrorCS")])]})])],"derivedFrom":makeQuery(id+"F5.opExtrude","CAP_EDGE",EDGE,{"disambiguationData":[OSD([subQ0])],"isStart":false})});}
            fillet(context, id + "F8", {"entities" : qUnion([Q0, Q1, Q2, Q3, Q4, Q5, Q6, Q7, Q8]), "radius" : 1.02 * mm, "tangentPropagation" : true, "allowEdgeOverflow" : false});
        }
        {
            var Q0;
            {var subQ0=sQuery(id+"F4.wireOp",EDGE,"E2");Q0=makeQuery(id+"F7.boolean.opBoolean","SPLIT",EDGE,{"disambiguationData":[TD([makeQuery(id+"F7.opExtrude","SWEPT_FACE",FACE,{"disambiguationData":[OSD([sQuery(id+"F6.wireOp",EDGE,"E35.MirrorCS")])]})])],"derivedFrom":makeQuery(id+"F5.opExtrude","CAP_EDGE",EDGE,{"disambiguationData":[OSD([subQ0])],"isStart":false})});}
            var Q1;
            {var subQ0=sQuery(id+"F4.wireOp",EDGE,"E2");Q1=makeQuery(id+"F7.boolean.opBoolean","SPLIT",EDGE,{"disambiguationData":[TD([makeQuery(id+"F7.opExtrude","SWEPT_FACE",FACE,{"disambiguationData":[OSD([sQuery(id+"F6.wireOp",EDGE,"E110.MirrorCS")])]})])],"derivedFrom":makeQuery(id+"F5.opExtrude","CAP_EDGE",EDGE,{"disambiguationData":[OSD([subQ0])],"isStart":false})});}
            var Q2;
            {var subQ0=sQuery(id+"F4.wireOp",EDGE,"E2");Q2=makeQuery(id+"F7.boolean.opBoolean","SPLIT",EDGE,{"disambiguationData":[TD([makeQuery(id+"F7.opExtrude","SWEPT_FACE",FACE,{"disambiguationData":[OSD([sQuery(id+"F6.wireOp",EDGE,"E97.MirrorCS")])]})])],"derivedFrom":makeQuery(id+"F5.opExtrude","CAP_EDGE",EDGE,{"disambiguationData":[OSD([subQ0])],"isStart":false})});}
            var Q3;
            {var subQ0=sQuery(id+"F4.wireOp",EDGE,"E2");Q3=makeQuery(id+"F7.boolean.opBoolean","SPLIT",EDGE,{"disambiguationData":[TD([makeQuery(id+"F7.opExtrude","SWEPT_FACE",FACE,{"disambiguationData":[OSD([sQuery(id+"F6.wireOp",EDGE,"E102.MirrorCS")])]})])],"derivedFrom":makeQuery(id+"F5.opExtrude","CAP_EDGE",EDGE,{"disambiguationData":[OSD([subQ0])],"isStart":false})});}
            var Q4;
            {var subQ0=sQuery(id+"F4.wireOp",EDGE,"E2");Q4=makeQuery(id+"F7.boolean.opBoolean","SPLIT",EDGE,{"disambiguationData":[TD([makeQuery(id+"F7.opExtrude","SWEPT_FACE",FACE,{"disambiguationData":[OSD([sQuery(id+"F6.wireOp",EDGE,"E109.MirrorCS")])]})])],"derivedFrom":makeQuery(id+"F5.opExtrude","CAP_EDGE",EDGE,{"disambiguationData":[OSD([subQ0])],"isStart":false})});}
            var Q5;
            {var subQ0=sQuery(id+"F4.wireOp",EDGE,"E2");Q5=makeQuery(id+"F7.boolean.opBoolean","SPLIT",EDGE,{"disambiguationData":[TD([makeQuery(id+"F7.opExtrude","SWEPT_FACE",FACE,{"disambiguationData":[OSD([sQuery(id+"F6.wireOp",EDGE,"E103.MirrorCS")])]})])],"derivedFrom":makeQuery(id+"F5.opExtrude","CAP_EDGE",EDGE,{"disambiguationData":[OSD([subQ0])],"isStart":false})});}
            var Q6;
            {var subQ0=sQuery(id+"F4.wireOp",EDGE,"E2");Q6=makeQuery(id+"F7.boolean.opBoolean","SPLIT",EDGE,{"disambiguationData":[TD([makeQuery(id+"F7.opExtrude","SWEPT_FACE",FACE,{"disambiguationData":[OSD([sQuery(id+"F6.wireOp",EDGE,"E106.MirrorCS")])]})])],"derivedFrom":makeQuery(id+"F5.opExtrude","CAP_EDGE",EDGE,{"disambiguationData":[OSD([subQ0])],"isStart":false})});}
            var Q7;
            {var subQ0=sQuery(id+"F4.wireOp",EDGE,"E2");Q7=makeQuery(id+"F7.boolean.opBoolean","SPLIT",EDGE,{"disambiguationData":[TD([makeQuery(id+"F7.opExtrude","SWEPT_FACE",FACE,{"disambiguationData":[OSD([sQuery(id+"F6.wireOp",EDGE,"E114.MirrorCS")])]})])],"derivedFrom":makeQuery(id+"F5.opExtrude","CAP_EDGE",EDGE,{"disambiguationData":[OSD([subQ0])],"isStart":false})});}
            var Q8;
            {var subQ0=sQuery(id+"F4.wireOp",EDGE,"E2");Q8=makeQuery(id+"F7.boolean.opBoolean","SPLIT",EDGE,{"disambiguationData":[TD([makeQuery(id+"F7.opExtrude","SWEPT_FACE",FACE,{"disambiguationData":[OSD([sQuery(id+"F6.wireOp",EDGE,"E87.MirrorCS")])]})])],"derivedFrom":makeQuery(id+"F5.opExtrude","CAP_EDGE",EDGE,{"disambiguationData":[OSD([subQ0])],"isStart":false})});}
            var Q9;
            {var subQ0=sQuery(id+"F4.wireOp",EDGE,"E2");Q9=makeQuery(id+"F7.boolean.opBoolean","SPLIT",EDGE,{"disambiguationData":[TD([makeQuery(id+"F7.opExtrude","SWEPT_FACE",FACE,{"disambiguationData":[OSD([sQuery(id+"F6.wireOp",EDGE,"E111.MirrorCS")])]})])],"derivedFrom":makeQuery(id+"F5.opExtrude","CAP_EDGE",EDGE,{"disambiguationData":[OSD([subQ0])],"isStart":false})});}
            var Q10;
            {var subQ0=sQuery(id+"F4.wireOp",EDGE,"E2");Q10=makeQuery(id+"F7.boolean.opBoolean","SPLIT",EDGE,{"disambiguationData":[TD([makeQuery(id+"F7.opExtrude","SWEPT_FACE",FACE,{"disambiguationData":[OSD([sQuery(id+"F6.wireOp",EDGE,"E100.MirrorCS")])]})])],"derivedFrom":makeQuery(id+"F5.opExtrude","CAP_EDGE",EDGE,{"disambiguationData":[OSD([subQ0])],"isStart":false})});}
            var Q11;
            {var subQ0=sQuery(id+"F4.wireOp",EDGE,"E2");Q11=makeQuery(id+"F7.boolean.opBoolean","SPLIT",EDGE,{"disambiguationData":[TD([makeQuery(id+"F7.opExtrude","SWEPT_FACE",FACE,{"disambiguationData":[OSD([sQuery(id+"F6.wireOp",EDGE,"E3.right")])]})])],"derivedFrom":makeQuery(id+"F5.opExtrude","CAP_EDGE",EDGE,{"disambiguationData":[OSD([subQ0])],"isStart":false})});}
            var Q12;
            {var subQ0=sQuery(id+"F4.wireOp",EDGE,"E2");Q12=makeQuery(id+"F7.boolean.opBoolean","SPLIT",EDGE,{"disambiguationData":[TD([makeQuery(id+"F7.opExtrude","SWEPT_FACE",FACE,{"disambiguationData":[OSD([sQuery(id+"F6.wireOp",EDGE,"E3.left")])]})])],"derivedFrom":makeQuery(id+"F5.opExtrude","CAP_EDGE",EDGE,{"disambiguationData":[OSD([subQ0])],"isStart":false})});}
            var Q13;
            {var subQ0=sQuery(id+"F4.wireOp",EDGE,"E2");Q13=makeQuery(id+"F7.boolean.opBoolean","SPLIT",EDGE,{"disambiguationData":[TD([makeQuery(id+"F7.opExtrude","SWEPT_FACE",FACE,{"disambiguationData":[OSD([sQuery(id+"F6.wireOp",EDGE,"E27.MirrorCS")])]})])],"derivedFrom":makeQuery(id+"F5.opExtrude","CAP_EDGE",EDGE,{"disambiguationData":[OSD([subQ0])],"isStart":false})});}
            var Q14;
            {var subQ0=sQuery(id+"F4.wireOp",EDGE,"E2");Q14=makeQuery(id+"F7.boolean.opBoolean","SPLIT",EDGE,{"disambiguationData":[TD([makeQuery(id+"F7.opExtrude","SWEPT_FACE",FACE,{"disambiguationData":[OSD([sQuery(id+"F6.wireOp",EDGE,"E32.MirrorCS")])]})])],"derivedFrom":makeQuery(id+"F5.opExtrude","CAP_EDGE",EDGE,{"disambiguationData":[OSD([subQ0])],"isStart":false})});}
            var Q15;
            {var subQ0=sQuery(id+"F4.wireOp",EDGE,"E2");Q15=makeQuery(id+"F7.boolean.opBoolean","SPLIT",EDGE,{"disambiguationData":[TD([makeQuery(id+"F7.opExtrude","SWEPT_FACE",FACE,{"disambiguationData":[OSD([sQuery(id+"F6.wireOp",EDGE,"E26.MirrorCS")])]})])],"derivedFrom":makeQuery(id+"F5.opExtrude","CAP_EDGE",EDGE,{"disambiguationData":[OSD([subQ0])],"isStart":false})});}
            var Q16;
            {var subQ0=sQuery(id+"F4.wireOp",EDGE,"E2");Q16=makeQuery(id+"F7.boolean.opBoolean","SPLIT",EDGE,{"disambiguationData":[TD([makeQuery(id+"F7.opExtrude","SWEPT_FACE",FACE,{"disambiguationData":[OSD([sQuery(id+"F6.wireOp",EDGE,"E29.MirrorCS")])]})])],"derivedFrom":makeQuery(id+"F5.opExtrude","CAP_EDGE",EDGE,{"disambiguationData":[OSD([subQ0])],"isStart":false})});}
            var Q17;
            {var subQ0=sQuery(id+"F4.wireOp",EDGE,"E2");Q17=makeQuery(id+"F7.boolean.opBoolean","SPLIT",EDGE,{"disambiguationData":[TD([makeQuery(id+"F7.opExtrude","SWEPT_FACE",FACE,{"disambiguationData":[OSD([sQuery(id+"F6.wireOp",EDGE,"E33.MirrorCS")])]})])],"derivedFrom":makeQuery(id+"F5.opExtrude","CAP_EDGE",EDGE,{"disambiguationData":[OSD([subQ0])],"isStart":false})});}
            var Q18;
            {var subQ0=sQuery(id+"F4.wireOp",EDGE,"E2");Q18=makeQuery(id+"F7.boolean.opBoolean","SPLIT",EDGE,{"disambiguationData":[TD([makeQuery(id+"F7.opExtrude","SWEPT_FACE",FACE,{"disambiguationData":[OSD([sQuery(id+"F6.wireOp",EDGE,"E31.MirrorCS")])]})])],"derivedFrom":makeQuery(id+"F5.opExtrude","CAP_EDGE",EDGE,{"disambiguationData":[OSD([subQ0])],"isStart":false})});}
            var Q19;
            {var subQ0=sQuery(id+"F4.wireOp",EDGE,"E2");Q19=makeQuery(id+"F7.boolean.opBoolean","SPLIT",EDGE,{"disambiguationData":[TD([makeQuery(id+"F7.opExtrude","SWEPT_FACE",FACE,{"disambiguationData":[OSD([sQuery(id+"F6.wireOp",EDGE,"E34.MirrorCS")])]})])],"derivedFrom":makeQuery(id+"F5.opExtrude","CAP_EDGE",EDGE,{"disambiguationData":[OSD([subQ0])],"isStart":false})});}
            var Q20;
            {var subQ0=sQuery(id+"F4.wireOp",EDGE,"E2");Q20=makeQuery(id+"F7.boolean.opBoolean","SPLIT",EDGE,{"disambiguationData":[TD([makeQuery(id+"F7.opExtrude","SWEPT_FACE",FACE,{"disambiguationData":[OSD([sQuery(id+"F6.wireOp",EDGE,"E28.MirrorCS")])]})])],"derivedFrom":makeQuery(id+"F5.opExtrude","CAP_EDGE",EDGE,{"disambiguationData":[OSD([subQ0])],"isStart":false})});}
            fillet(context, id + "F9", {"entities" : qUnion([Q0, Q1, Q2, Q3, Q4, Q5, Q6, Q7, Q8, Q9, Q10, Q11, Q12, Q13, Q14, Q15, Q16, Q17, Q18, Q19, Q20]), "radius" : 0.76 * mm, "tangentPropagation" : true, "allowEdgeOverflow" : false});
        }
        {
            var Q0;
            {var subQ0=sQuery(id+"F4.wireOp",EDGE,"E2");Q0=makeQuery(id+"F7.boolean.opBoolean","SPLIT",EDGE,{"disambiguationData":[TD([makeQuery(id+"F7.opExtrude","SWEPT_FACE",FACE,{"disambiguationData":[OSD([sQuery(id+"F6.wireOp",EDGE,"E4.4.0.1")])]})])],"derivedFrom":makeQuery(id+"F5.opExtrude","CAP_EDGE",EDGE,{"disambiguationData":[OSD([subQ0])],"isStart":false})});}
            var Q1;
            {var subQ0=sQuery(id+"F4.wireOp",EDGE,"E2");Q1=makeQuery(id+"F7.boolean.opBoolean","SPLIT",EDGE,{"disambiguationData":[TD([makeQuery(id+"F7.opExtrude","SWEPT_FACE",FACE,{"disambiguationData":[OSD([sQuery(id+"F6.wireOp",EDGE,"E4.3.0.1")])]})])],"derivedFrom":makeQuery(id+"F5.opExtrude","CAP_EDGE",EDGE,{"disambiguationData":[OSD([subQ0])],"isStart":false})});}
            var Q2;
            {var subQ0=sQuery(id+"F4.wireOp",EDGE,"E2");Q2=makeQuery(id+"F7.boolean.opBoolean","SPLIT",EDGE,{"disambiguationData":[TD([makeQuery(id+"F7.opExtrude","SWEPT_FACE",FACE,{"disambiguationData":[OSD([sQuery(id+"F6.wireOp",EDGE,"E4.2.0.1")])]})])],"derivedFrom":makeQuery(id+"F5.opExtrude","CAP_EDGE",EDGE,{"disambiguationData":[OSD([subQ0])],"isStart":false})});}
            var Q3;
            {var subQ0=sQuery(id+"F4.wireOp",EDGE,"E2");Q3=makeQuery(id+"F7.boolean.opBoolean","SPLIT",EDGE,{"disambiguationData":[TD([makeQuery(id+"F7.opExtrude","SWEPT_FACE",FACE,{"disambiguationData":[OSD([sQuery(id+"F6.wireOp",EDGE,"E4.1.0.1")])]})])],"derivedFrom":makeQuery(id+"F5.opExtrude","CAP_EDGE",EDGE,{"disambiguationData":[OSD([subQ0])],"isStart":false})});}
            var Q4;
            {var subQ0=sQuery(id+"F4.wireOp",EDGE,"E2");Q4=makeQuery(id+"F7.boolean.opBoolean","SPLIT",EDGE,{"disambiguationData":[TD([makeQuery(id+"F7.opExtrude","SWEPT_FACE",FACE,{"disambiguationData":[OSD([sQuery(id+"F6.wireOp",EDGE,"E108.MirrorCS")])]})])],"derivedFrom":makeQuery(id+"F5.opExtrude","CAP_EDGE",EDGE,{"disambiguationData":[OSD([subQ0])],"isStart":false})});}
            var Q5;
            {var subQ0=sQuery(id+"F4.wireOp",EDGE,"E2");Q5=makeQuery(id+"F7.boolean.opBoolean","SPLIT",EDGE,{"disambiguationData":[TD([makeQuery(id+"F7.opExtrude","SWEPT_FACE",FACE,{"disambiguationData":[OSD([sQuery(id+"F6.wireOp",EDGE,"E96.MirrorCS")])]})])],"derivedFrom":makeQuery(id+"F5.opExtrude","CAP_EDGE",EDGE,{"disambiguationData":[OSD([subQ0])],"isStart":false})});}
            var Q6;
            {var subQ0=sQuery(id+"F4.wireOp",EDGE,"E2");Q6=makeQuery(id+"F7.boolean.opBoolean","SPLIT",EDGE,{"disambiguationData":[TD([makeQuery(id+"F7.opExtrude","SWEPT_FACE",FACE,{"disambiguationData":[OSD([sQuery(id+"F6.wireOp",EDGE,"E98.MirrorCS")])]})])],"derivedFrom":makeQuery(id+"F5.opExtrude","CAP_EDGE",EDGE,{"disambiguationData":[OSD([subQ0])],"isStart":false})});}
            var Q7;
            {var subQ0=sQuery(id+"F4.wireOp",EDGE,"E2");Q7=makeQuery(id+"F7.boolean.opBoolean","SPLIT",EDGE,{"disambiguationData":[TD([makeQuery(id+"F7.opExtrude","SWEPT_FACE",FACE,{"disambiguationData":[OSD([sQuery(id+"F6.wireOp",EDGE,"E99.MirrorCS")])]})])],"derivedFrom":makeQuery(id+"F5.opExtrude","CAP_EDGE",EDGE,{"disambiguationData":[OSD([subQ0])],"isStart":false})});}
            fillet(context, id + "F10", {"entities" : qUnion([Q0, Q1, Q2, Q3, Q4, Q5, Q6, Q7]), "radius" : 0.89 * mm, "tangentPropagation" : true, "allowEdgeOverflow" : false});
        }
        {
            var Q0;
            Q0=makeQuery(id+"F5.opExtrude","CAP_FACE",FACE,{"disambiguationData":[OSD([sQuery(id+"F4.wireOp",EDGE,"E2")])],"isStart":false});
            var sketch = newSketch(context, id + "F11", { "sketchPlane" : qUnion([Q0])});
            skLineSegment(sketch, "E153", {"start": v(-25.53, 0) * mm, "end": v(-0.63, 0) * mm, "construction": true});
            skLineSegment(sketch, "E154", {"start": v(-0.64, 0) * mm, "end": v(24.26, 0) * mm, "construction": true});
            skCircle(sketch, "E155", {"center": v(-25.53, 0) * mm, "radius": 2.58 * mm});
            skCircle(sketch, "E156", {"center": v(-0.64, 0) * mm, "radius": 2.58 * mm});
            skCircle(sketch, "E157", {"center": v(24.26, 0) * mm, "radius": 2.58 * mm});
            skSolve(sketch);
        }
        {
            var Q0;
            Q0=makeQuery(id+"F11.imprint","IMPRINT",FACE,{"disambiguationData":[TD([[makeQuery(id+"F11.imprint","IMPRINT",EDGE,{"derivedFrom":sQuery(id+"F11.wireOp",EDGE,"E156")}),1.0]])]});
            var Q1;
            {var subQ0=sQuery(id+"F11.wireOp",EDGE,"E157");var subQ1=sQuery(id+"F4.wireOp",EDGE,"E2");var subQ2=makeQuery(id+"F5.opExtrude","CAP_FACE",FACE,{"disambiguationData":[OSD([subQ1])],"isStart":false});var subQ3=subQ2;var subQ4=makeQuery(id+"F7.boolean.opBoolean","SPLIT",EDGE,{"disambiguationData":[TD([makeQuery(id+"F7.opExtrude","SWEPT_FACE",FACE,{"disambiguationData":[OSD([sQuery(id+"F6.wireOp",EDGE,"E4.9.0.1")])]})])],"derivedFrom":makeQuery(id+"F5.opExtrude","CAP_EDGE",EDGE,{"disambiguationData":[OSD([subQ1])],"isStart":false})});var subQ5=makeQuery(id+"F8.opFillet","BLEND_EDGE",EDGE,{"disambiguationData":[OD(0.0)],"blendedFrom":[subQ4,subQ3],"blendedInto":[subQ3]});var subQ6=makeQuery(id+"F11.imprint","INTERSECT",VERTEX,{"disambiguationData":[OD(0.0)],"derivedFrom":[subQ5,subQ0]});Q1=makeQuery(id+"F11.imprint","IMPRINT",FACE,{"disambiguationData":[TD([[makeQuery(id+"F11.imprint","IMPRINT",EDGE,{"disambiguationData":[TD([[subQ6,-1.0]])],"derivedFrom":subQ0}),1.0]])]});}
            var Q2;
            {var subQ0=sQuery(id+"F11.wireOp",EDGE,"E157");var subQ1=sQuery(id+"F4.wireOp",EDGE,"E2");var subQ2=makeQuery(id+"F5.opExtrude","CAP_FACE",FACE,{"disambiguationData":[OSD([subQ1])],"isStart":false});var subQ3=makeQuery(id+"F8.opFillet","BLEND_EDGE",EDGE,{"disambiguationData":[OD(0.0)],"blendedFrom":[makeQuery(id+"F7.boolean.opBoolean","SPLIT",EDGE,{"disambiguationData":[TD([makeQuery(id+"F7.opExtrude","SWEPT_FACE",FACE,{"disambiguationData":[OSD([sQuery(id+"F6.wireOp",EDGE,"E4.9.0.1")])]})])],"derivedFrom":makeQuery(id+"F5.opExtrude","CAP_EDGE",EDGE,{"disambiguationData":[OSD([subQ1])],"isStart":false})}),subQ2],"blendedInto":[subQ2]});var subQ4=makeQuery(id+"F11.imprint","INTERSECT",VERTEX,{"disambiguationData":[OD(0.0)],"derivedFrom":[subQ3,subQ0]});Q2=makeQuery(id+"F11.imprint","IMPRINT",FACE,{"disambiguationData":[TD([[makeQuery(id+"F11.imprint","IMPRINT",EDGE,{"disambiguationData":[TD([[subQ4,1.0]])],"derivedFrom":subQ0}),1.0]])]});}
            var Q3;
            {var subQ0=sQuery(id+"F11.wireOp",EDGE,"E157");var subQ1=sQuery(id+"F4.wireOp",EDGE,"E2");var subQ2=makeQuery(id+"F5.opExtrude","CAP_FACE",FACE,{"disambiguationData":[OSD([subQ1])],"isStart":false});var subQ3=makeQuery(id+"F8.opFillet","BLEND_EDGE",EDGE,{"disambiguationData":[OD(1.0)],"blendedFrom":[makeQuery(id+"F7.boolean.opBoolean","SPLIT",EDGE,{"disambiguationData":[TD([makeQuery(id+"F7.opExtrude","SWEPT_FACE",FACE,{"disambiguationData":[OSD([sQuery(id+"F6.wireOp",EDGE,"E4.9.0.1")])]})])],"derivedFrom":makeQuery(id+"F5.opExtrude","CAP_EDGE",EDGE,{"disambiguationData":[OSD([subQ1])],"isStart":false})}),subQ2],"blendedInto":[subQ2]});var subQ4=makeQuery(id+"F11.imprint","INTERSECT",VERTEX,{"disambiguationData":[OD(0.0)],"derivedFrom":[subQ3,subQ0]});Q3=makeQuery(id+"F11.imprint","IMPRINT",FACE,{"disambiguationData":[TD([[makeQuery(id+"F11.imprint","IMPRINT",EDGE,{"disambiguationData":[TD([[subQ4,-1.0]])],"derivedFrom":subQ0}),1.0]])]});}
            var Q4;
            {var subQ0=sQuery(id+"F11.wireOp",EDGE,"E155");var subQ1=sQuery(id+"F4.wireOp",EDGE,"E2");var subQ2=makeQuery(id+"F5.opExtrude","CAP_FACE",FACE,{"disambiguationData":[OSD([subQ1])],"isStart":false});var subQ3=subQ2;var subQ4=makeQuery(id+"F7.boolean.opBoolean","SPLIT",EDGE,{"disambiguationData":[TD([makeQuery(id+"F7.opExtrude","SWEPT_FACE",FACE,{"disambiguationData":[OSD([sQuery(id+"F6.wireOp",EDGE,"E35.MirrorCS")])]})])],"derivedFrom":makeQuery(id+"F5.opExtrude","CAP_EDGE",EDGE,{"disambiguationData":[OSD([subQ1])],"isStart":false})});var subQ5=makeQuery(id+"F9.opFillet","BLEND_EDGE",EDGE,{"disambiguationData":[OD(0.0)],"blendedFrom":[subQ4,subQ3],"blendedInto":[subQ3]});var subQ6=makeQuery(id+"F11.imprint","INTERSECT",VERTEX,{"disambiguationData":[OD(0.0)],"derivedFrom":[subQ5,subQ0]});Q4=makeQuery(id+"F11.imprint","IMPRINT",FACE,{"disambiguationData":[TD([[makeQuery(id+"F11.imprint","IMPRINT",EDGE,{"disambiguationData":[TD([[subQ6,-1.0]])],"derivedFrom":subQ0}),1.0]])]});}
            var Q5;
            {var subQ0=sQuery(id+"F11.wireOp",EDGE,"E155");var subQ1=sQuery(id+"F4.wireOp",EDGE,"E2");var subQ2=makeQuery(id+"F5.opExtrude","CAP_FACE",FACE,{"disambiguationData":[OSD([subQ1])],"isStart":false});var subQ3=makeQuery(id+"F9.opFillet","BLEND_EDGE",EDGE,{"disambiguationData":[OD(0.0)],"blendedFrom":[makeQuery(id+"F7.boolean.opBoolean","SPLIT",EDGE,{"disambiguationData":[TD([makeQuery(id+"F7.opExtrude","SWEPT_FACE",FACE,{"disambiguationData":[OSD([sQuery(id+"F6.wireOp",EDGE,"E35.MirrorCS")])]})])],"derivedFrom":makeQuery(id+"F5.opExtrude","CAP_EDGE",EDGE,{"disambiguationData":[OSD([subQ1])],"isStart":false})}),subQ2],"blendedInto":[subQ2]});var subQ4=makeQuery(id+"F11.imprint","INTERSECT",VERTEX,{"disambiguationData":[OD(0.0)],"derivedFrom":[subQ3,subQ0]});Q5=makeQuery(id+"F11.imprint","IMPRINT",FACE,{"disambiguationData":[TD([[makeQuery(id+"F11.imprint","IMPRINT",EDGE,{"disambiguationData":[TD([[subQ4,1.0]])],"derivedFrom":subQ0}),1.0]])]});}
            var Q6;
            {var subQ0=sQuery(id+"F11.wireOp",EDGE,"E155");var subQ1=sQuery(id+"F4.wireOp",EDGE,"E2");var subQ2=makeQuery(id+"F5.opExtrude","CAP_FACE",FACE,{"disambiguationData":[OSD([subQ1])],"isStart":false});var subQ3=makeQuery(id+"F9.opFillet","BLEND_EDGE",EDGE,{"disambiguationData":[OD(1.0)],"blendedFrom":[makeQuery(id+"F7.boolean.opBoolean","SPLIT",EDGE,{"disambiguationData":[TD([makeQuery(id+"F7.opExtrude","SWEPT_FACE",FACE,{"disambiguationData":[OSD([sQuery(id+"F6.wireOp",EDGE,"E35.MirrorCS")])]})])],"derivedFrom":makeQuery(id+"F5.opExtrude","CAP_EDGE",EDGE,{"disambiguationData":[OSD([subQ1])],"isStart":false})}),subQ2],"blendedInto":[subQ2]});var subQ4=makeQuery(id+"F11.imprint","INTERSECT",VERTEX,{"disambiguationData":[OD(0.0)],"derivedFrom":[subQ3,subQ0]});Q6=makeQuery(id+"F11.imprint","IMPRINT",FACE,{"disambiguationData":[TD([[makeQuery(id+"F11.imprint","IMPRINT",EDGE,{"disambiguationData":[TD([[subQ4,-1.0]])],"derivedFrom":subQ0}),1.0]])]});}
            extrude(context, id + "F12", {"entities" : qUnion([Q0, Q1, Q2, Q3, Q4, Q5, Q6]), "operationType" : NewBodyOperationType.REMOVE, "oppositeDirection" : true, "depth" : 5.84 * mm, "offsetDistance" : 25.4 * mm});
        }
        {
            var Q0;
            Q0=makeQuery(id+"F3.opLoft","CAP_FACE",FACE,{"disambiguationData":[OSD([makeQuery(id+"F0.imprint","IMPRINT",FACE,{"disambiguationData":[TD([[makeQuery(id+"F0.imprint","IMPRINT",EDGE,{"derivedFrom":sQuery(id+"F0.wireOp",EDGE,"E0")}),1.0]])]})])],"isStart":true});
            var sketch = newSketch(context, id + "F13", { "sketchPlane" : qUnion([Q0])});
            skLineSegment(sketch, "E158", {"start": v(-25.64, 0) * mm, "end": v(-0.24, 0) * mm, "construction": true});
            skLineSegment(sketch, "E159", {"start": v(-0.24, 0) * mm, "end": v(25.16, 0) * mm, "construction": true});
            skCircle(sketch, "E160", {"center": v(-25.64, 0) * mm, "radius": 2.62 * mm});
            skCircle(sketch, "E161", {"center": v(-0.24, 0) * mm, "radius": 2.62 * mm});
            skCircle(sketch, "E162", {"center": v(25.16, 0) * mm, "radius": 2.62 * mm});
            skSolve(sketch);
        }
        {
            var Q0;
            Q0=makeQuery(id+"F13.imprint","IMPRINT",FACE,{"disambiguationData":[TD([[makeQuery(id+"F13.imprint","IMPRINT",EDGE,{"derivedFrom":sQuery(id+"F13.wireOp",EDGE,"E160")}),1.0]])]});
            var Q1;
            Q1=makeQuery(id+"F13.imprint","IMPRINT",FACE,{"disambiguationData":[TD([[makeQuery(id+"F13.imprint","IMPRINT",EDGE,{"derivedFrom":sQuery(id+"F13.wireOp",EDGE,"E162")}),1.0]])]});
            extrude(context, id + "F14", {"entities" : qUnion([Q0, Q1]), "operationType" : NewBodyOperationType.ADD, "depth" : 15 * mm, "offsetDistance" : 25.4 * mm});
        }
        {
            var Q0;
            Q0=makeQuery(id+"F14.opExtrude","CAP_EDGE",EDGE,{"disambiguationData":[OSD([sQuery(id+"F13.wireOp",EDGE,"E160")])],"isStart":false});
            var Q1;
            Q1=makeQuery(id+"F14.opExtrude","CAP_EDGE",EDGE,{"disambiguationData":[OSD([sQuery(id+"F13.wireOp",EDGE,"E162")])],"isStart":false});
            chamfer(context, id + "F15", {"entities" : qUnion([Q0, Q1]), "chamferType" : ChamferType.TWO_OFFSETS, "width1" : 0.73 * mm, "oppositeDirection" : false, "width2" : 4.76 * mm, "tangentPropagation" : true});
        }
        {
            var Q0;
            {var subQ31=sQuery(id+"F4.wireOp",EDGE,"E2");var subQ33=makeQuery(id+"F5.opExtrude","CAP_FACE",FACE,{"disambiguationData":[OSD([subQ31])],"isStart":false});Q0=makeQuery(id+"F12.boolean.opBoolean","SPLIT",FACE,{"disambiguationData":[TD([makeQuery(id+"F7.boolean.opBoolean","COPY",FACE,{"derivedFrom":makeQuery(id+"F7.opExtrude","SWEPT_FACE",FACE,{"disambiguationData":[OSD([sQuery(id+"F6.wireOp",EDGE,"E3.bottom")])]})})])],"derivedFrom":subQ33});}
            var sketch = newSketch(context, id + "F16", { "sketchPlane" : qUnion([Q0])});
            skEllipse(sketch, "E163", {"center": v(-13.93, 0) * mm, "majorRadius": 5.08 * mm, "minorRadius": 2.54 * mm, "majorAxis": v(1, 0)});
            skSolve(sketch);
        }
        {
            var Q0;
            Q0=makeQuery(id+"F16.imprint","IMPRINT",FACE,{"disambiguationData":[TD([[makeQuery(id+"F16.imprint","IMPRINT",EDGE,{"derivedFrom":sQuery(id+"F16.wireOp",EDGE,"E163")}),1.0]])]});
            extrude(context, id + "F17", {"entities" : qUnion([Q0]), "operationType" : NewBodyOperationType.ADD, "depth" : 3.8 * mm, "offsetDistance" : 25.4 * mm});
        }
        {
            var Q0;
            Q0=makeQuery(id+"F17.opExtrude","CAP_EDGE",EDGE,{"disambiguationData":[OSD([sQuery(id+"F16.wireOp",EDGE,"E163")])],"isStart":false});
            fillet(context, id + "F18", {"entities" : qUnion([Q0]), "tangentPropagation" : true, "radius" : 1.24 * mm, "defaultsChanged" : true, "vertexSettings" : [], "allowEdgeOverflow" : false});
        }
    });
